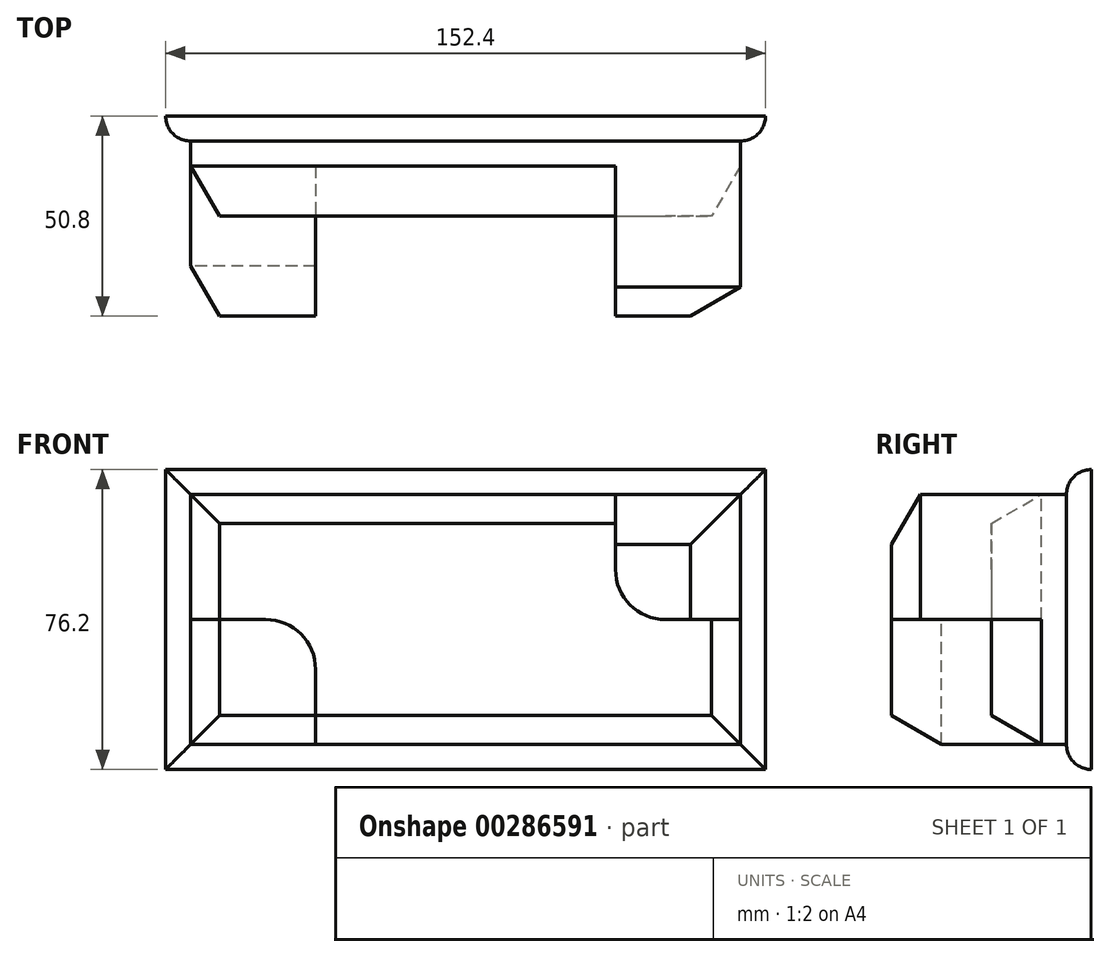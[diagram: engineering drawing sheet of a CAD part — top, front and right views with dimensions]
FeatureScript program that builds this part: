
annotation { "Feature Type Name" : "Feature", "Feature Type Description" : "" }
export const myFeature = defineFeature(function(context is Context, id is Id, definition is map)
    precondition{}
    {
        {
            var Q0;
            Q0=qCreatedBy(makeId("Front.planeOp"),FACE);
            var sketch = newSketch(context, id + "F0", { "sketchPlane" : qUnion([Q0])});
            skLineSegment(sketch, "E0.bottom", {"start": v(0, 0) * mm, "end": v(152.4, 0) * mm});
            skLineSegment(sketch, "E0.top", {"start": v(0, -76.2) * mm, "end": v(152.4, -76.2) * mm});
            skLineSegment(sketch, "E0.left", {"start": v(0, 0) * mm, "end": v(0, -76.2) * mm});
            skLineSegment(sketch, "E0.right", {"start": v(152.4, 0) * mm, "end": v(152.4, -76.2) * mm});
            skLineSegment(sketch, "E1.0", {"start": v(6.35, -6.35) * mm, "end": v(146.05, -6.35) * mm});
            skLineSegment(sketch, "E1.1", {"start": v(6.35, -6.35) * mm, "end": v(6.35, -69.85) * mm});
            skLineSegment(sketch, "E1.2", {"start": v(6.35, -69.85) * mm, "end": v(146.05, -69.85) * mm});
            skLineSegment(sketch, "E1.3", {"start": v(146.05, -6.35) * mm, "end": v(146.05, -69.85) * mm});
            skPoint(sketch, "E2", {"position": v(6.35, -38.1) * mm});
            skLineSegment(sketch, "E3", {"start": v(6.35, -38.1) * mm, "end": v(25.4, -38.1) * mm});
            skLineSegment(sketch, "E4", {"start": v(38.1, -50.8) * mm, "end": v(38.1, -69.85) * mm});
            skPoint(sketch, "E5.visualSharp", {"position": v(38.1, -38.1) * mm});
            skArc(sketch, "E5.filletArc", {"start": v(38.1, -50.8) * mm, "mid": v(34.38, -41.82) * mm, "end": v(25.4, -38.1) * mm});
            skLineSegment(sketch, "E6", {"start": v(146.05, -38.1) * mm, "end": v(127, -38.1) * mm});
            skPoint(sketch, "E6.endSnap0", {"position": v(146.05, -38.1) * mm});
            skLineSegment(sketch, "E7", {"start": v(114.3, -25.4) * mm, "end": v(114.3, -6.35) * mm});
            skPoint(sketch, "E8.visualSharp", {"position": v(114.3, -38.1) * mm});
            skArc(sketch, "E8.filletArc", {"start": v(114.3, -25.4) * mm, "mid": v(118.02, -34.38) * mm, "end": v(127, -38.1) * mm});
            skSolve(sketch);
        }
        {
            var Q0;
            {var subQ7=sQuery(id+"F0.wireOp",EDGE,"E3");Q0=makeQuery(id+"F0.imprint","IMPRINT",FACE,{"disambiguationData":[TD([[makeQuery(id+"F0.imprint","IMPRINT",EDGE,{"derivedFrom":subQ7}),1.0]])]});}
            extrude(context, id + "F1", {"entities" : qUnion([Q0]), "depth" : 25.4 * mm});
        }
        {
            var Q0;
            Q0 = qSketchRegion(id + "F0", true);
            extrude(context, id + "F2", {"entities" : qUnion([Q0]), "operationType" : NewBodyOperationType.ADD, "depth" : 6.35 * mm});
        }
        {
            var Q0;
            {var subQ4=sQuery(id+"F0.wireOp",EDGE,"E3");Q0=makeQuery(id+"F0.imprint","IMPRINT",FACE,{"disambiguationData":[TD([[makeQuery(id+"F0.imprint","IMPRINT",EDGE,{"derivedFrom":subQ4}),-1.0]])]});}
            var Q1;
            {var subQ4=sQuery(id+"F0.wireOp",EDGE,"E6");Q1=makeQuery(id+"F0.imprint","IMPRINT",FACE,{"disambiguationData":[TD([[makeQuery(id+"F0.imprint","IMPRINT",EDGE,{"derivedFrom":subQ4}),-1.0]])]});}
            extrude(context, id + "F3", {"entities" : qUnion([Q0, Q1]), "operationType" : NewBodyOperationType.ADD, "depth" : 50.8 * mm});
        }
        {
            var Q0;
            Q0=makeQuery(id+"F2.opExtrude","CAP_EDGE",EDGE,{"disambiguationData":[OSD([sQuery(id+"F0.wireOp",EDGE,"E0.top")])],"isStart":false});
            var Q1;
            Q1=makeQuery(id+"F2.opExtrude","CAP_EDGE",EDGE,{"disambiguationData":[OSD([sQuery(id+"F0.wireOp",EDGE,"E0.left")])],"isStart":false});
            var Q2;
            Q2=makeQuery(id+"F2.opExtrude","CAP_EDGE",EDGE,{"disambiguationData":[OSD([sQuery(id+"F0.wireOp",EDGE,"E0.right")])],"isStart":false});
            var Q3;
            Q3=makeQuery(id+"F2.opExtrude","CAP_EDGE",EDGE,{"disambiguationData":[OSD([sQuery(id+"F0.wireOp",EDGE,"E0.bottom")])],"isStart":false});
            fillet(context, id + "F4", {"entities" : qUnion([Q0, Q1, Q2, Q3]), "radius" : 6.35 * mm, "tangentPropagation" : true, "allowEdgeOverflow" : false});
        }
        {
            var Q0;
            Q0=makeQuery(id+"F1.opExtrude","CAP_EDGE",EDGE,{"disambiguationData":[OSD([sQuery(id+"F0.wireOp",EDGE,"E1.2")])],"isStart":false});
            var Q1;
            Q1=makeQuery(id+"F3.opExtrude","CAP_EDGE",EDGE,{"disambiguationData":[OSD([sQuery(id+"F0.wireOp",EDGE,"E1.2")])],"isStart":false});
            var Q2;
            Q2=makeQuery(id+"F3.opExtrude","CAP_EDGE",EDGE,{"disambiguationData":[OSD([sQuery(id+"F0.wireOp",EDGE,"E1.1")])],"isStart":false});
            var Q3;
            Q3=makeQuery(id+"F1.opExtrude","CAP_EDGE",EDGE,{"disambiguationData":[OSD([sQuery(id+"F0.wireOp",EDGE,"E1.3")])],"isStart":false});
            var Q4;
            Q4=makeQuery(id+"F1.opExtrude","CAP_EDGE",EDGE,{"disambiguationData":[OSD([sQuery(id+"F0.wireOp",EDGE,"E1.1")])],"isStart":false});
            var Q5;
            Q5=makeQuery(id+"F1.opExtrude","CAP_EDGE",EDGE,{"disambiguationData":[OSD([sQuery(id+"F0.wireOp",EDGE,"E1.0")])],"isStart":false});
            var Q6;
            Q6=makeQuery(id+"F3.opExtrude","CAP_EDGE",EDGE,{"disambiguationData":[OSD([sQuery(id+"F0.wireOp",EDGE,"E1.0")])],"isStart":false});
            var Q7;
            Q7=makeQuery(id+"F3.opExtrude","CAP_EDGE",EDGE,{"disambiguationData":[OSD([sQuery(id+"F0.wireOp",EDGE,"E1.3")])],"isStart":false});
            chamfer(context, id + "F5", {"entities" : qUnion([Q0, Q1, Q2, Q3, Q4, Q5, Q6, Q7]), "chamferType" : ChamferType.OFFSET_ANGLE, "width" : 12.7 * mm, "oppositeDirection" : true, "angle" : 30 * degree, "tangentPropagation" : true});
        }
    });
